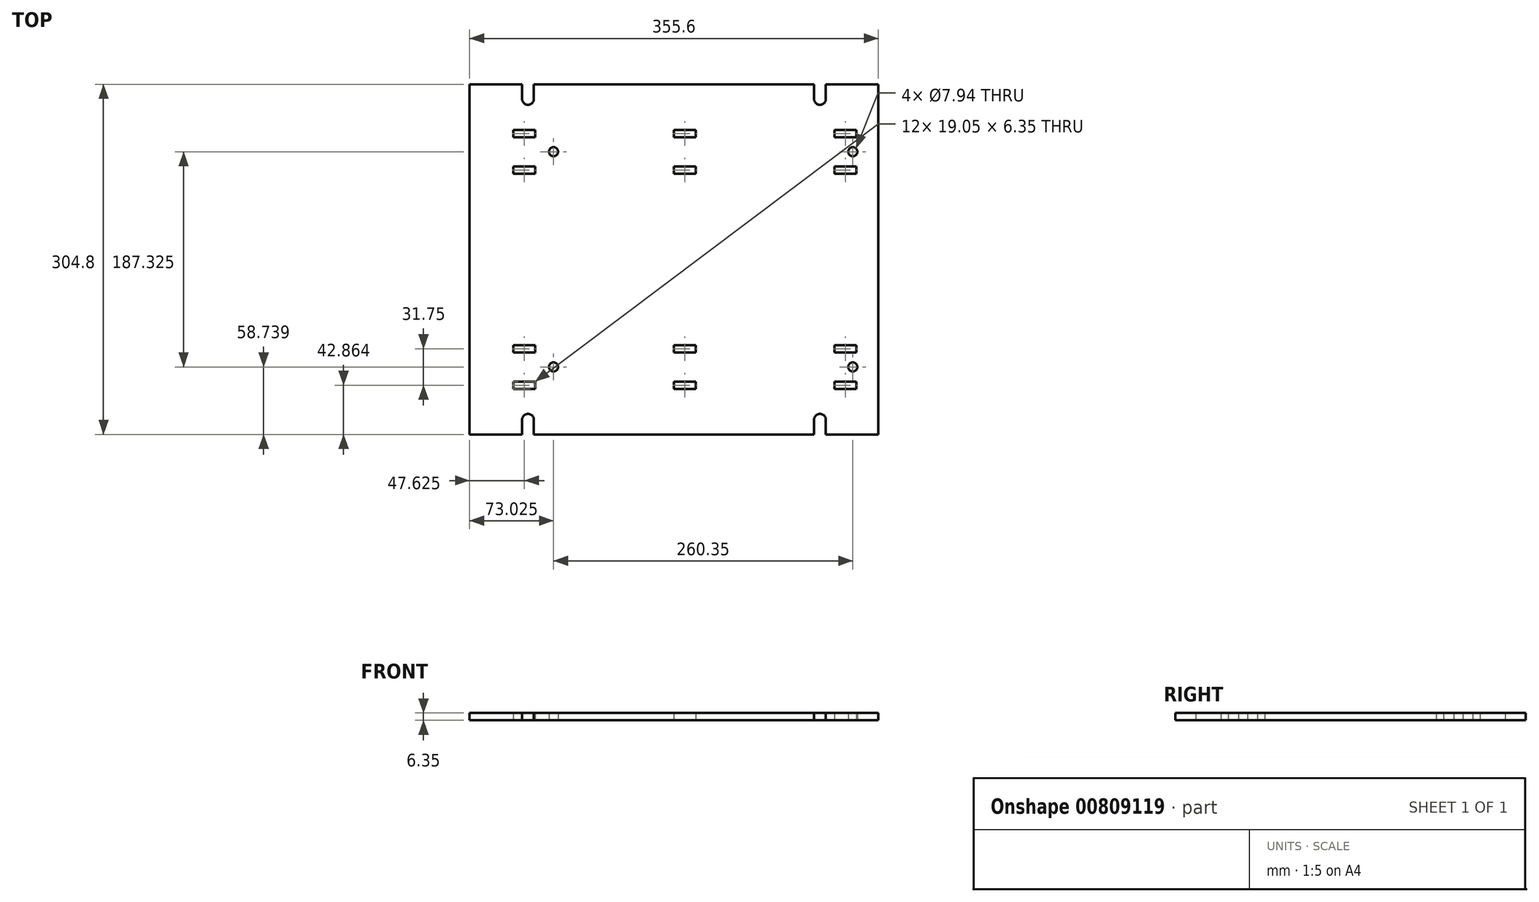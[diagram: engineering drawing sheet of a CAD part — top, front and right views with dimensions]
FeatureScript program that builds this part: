
annotation { "Feature Type Name" : "Feature", "Feature Type Description" : "" }
export const myFeature = defineFeature(function(context is Context, id is Id, definition is map)
    precondition{}
    {
        {
            var Q0;
            Q0=qCreatedBy(makeId("Top.planeOp"),FACE);
            var sketch = newSketch(context, id + "F0", { "sketchPlane" : qUnion([Q0])});
            skLineSegment(sketch, "E0.bottom", {"start": v(0, 4.6) * mm, "end": v(355.6, 4.6) * mm});
            skLineSegment(sketch, "E0.top", {"start": v(0, 309.4) * mm, "end": v(355.6, 309.4) * mm});
            skLineSegment(sketch, "E0.left", {"start": v(0, 4.6) * mm, "end": v(0, 309.4) * mm});
            skLineSegment(sketch, "E0.right", {"start": v(355.6, 4.6) * mm, "end": v(355.6, 309.4) * mm});
            skCircle(sketch, "E1", {"center": v(333.38, 63.33) * mm, "radius": 3.97 * mm});
            skCircle(sketch, "E2.0.1.0", {"center": v(333.38, 250.65) * mm, "radius": 3.97 * mm});
            skCircle(sketch, "E2.1.0.0", {"center": v(73.03, 63.33) * mm, "radius": 3.97 * mm});
            skCircle(sketch, "E2.1.1.0", {"center": v(73.03, 250.65) * mm, "radius": 3.97 * mm});
            skLineSegment(sketch, "E2.direction1", {"start": v(333.38, 63.33) * mm, "end": v(73.03, 63.33) * mm, "construction": true});
            skLineSegment(sketch, "E2.direction2", {"start": v(333.38, 63.33) * mm, "end": v(333.38, 250.65) * mm, "construction": true});
            skLineSegment(sketch, "E3.bottom", {"start": v(336.55, 44.28) * mm, "end": v(317.5, 44.28) * mm});
            skLineSegment(sketch, "E3.top", {"start": v(336.55, 50.63) * mm, "end": v(317.5, 50.63) * mm});
            skLineSegment(sketch, "E3.left", {"start": v(336.55, 44.28) * mm, "end": v(336.55, 50.63) * mm});
            skLineSegment(sketch, "E3.right", {"start": v(317.5, 44.28) * mm, "end": v(317.5, 50.63) * mm});
            skLineSegment(sketch, "E4.0.1.0", {"start": v(336.55, 82.38) * mm, "end": v(317.5, 82.38) * mm});
            skLineSegment(sketch, "E4.0.1.1", {"start": v(336.55, 76.03) * mm, "end": v(317.5, 76.03) * mm});
            skLineSegment(sketch, "E4.0.1.2", {"start": v(317.5, 76.03) * mm, "end": v(317.5, 82.38) * mm});
            skLineSegment(sketch, "E4.0.1.3", {"start": v(336.55, 76.03) * mm, "end": v(336.55, 82.38) * mm});
            skLineSegment(sketch, "E4.direction2", {"start": v(317.5, 50.63) * mm, "end": v(317.5, 82.38) * mm, "construction": true});
            skLineSegment(sketch, "E5.0.1.0", {"start": v(336.55, 269.7) * mm, "end": v(317.5, 269.7) * mm});
            skLineSegment(sketch, "E5.0.1.1", {"start": v(336.55, 263.35) * mm, "end": v(336.55, 269.7) * mm});
            skLineSegment(sketch, "E5.0.1.2", {"start": v(336.55, 263.35) * mm, "end": v(317.5, 263.35) * mm});
            skLineSegment(sketch, "E5.0.1.3", {"start": v(336.55, 231.6) * mm, "end": v(317.5, 231.6) * mm});
            skLineSegment(sketch, "E5.0.1.4", {"start": v(336.55, 231.6) * mm, "end": v(336.55, 237.95) * mm});
            skLineSegment(sketch, "E5.0.1.5", {"start": v(317.5, 231.6) * mm, "end": v(317.5, 237.95) * mm});
            skLineSegment(sketch, "E5.0.1.6", {"start": v(317.5, 263.35) * mm, "end": v(317.5, 269.7) * mm});
            skLineSegment(sketch, "E5.0.1.7", {"start": v(336.55, 237.95) * mm, "end": v(317.5, 237.95) * mm});
            skLineSegment(sketch, "E5.1.0.0", {"start": v(196.85, 82.38) * mm, "end": v(177.8, 82.38) * mm});
            skLineSegment(sketch, "E5.1.0.1", {"start": v(196.85, 76.03) * mm, "end": v(196.85, 82.38) * mm});
            skLineSegment(sketch, "E5.1.0.2", {"start": v(196.85, 76.03) * mm, "end": v(177.8, 76.03) * mm});
            skLineSegment(sketch, "E5.1.0.3", {"start": v(196.85, 44.28) * mm, "end": v(177.8, 44.28) * mm});
            skLineSegment(sketch, "E5.1.0.4", {"start": v(196.85, 44.28) * mm, "end": v(196.85, 50.63) * mm});
            skLineSegment(sketch, "E5.1.0.5", {"start": v(177.8, 44.28) * mm, "end": v(177.8, 50.63) * mm});
            skLineSegment(sketch, "E5.1.0.6", {"start": v(177.8, 76.03) * mm, "end": v(177.8, 82.38) * mm});
            skLineSegment(sketch, "E5.1.0.7", {"start": v(196.85, 50.63) * mm, "end": v(177.8, 50.63) * mm});
            skLineSegment(sketch, "E5.1.1.0", {"start": v(196.85, 269.7) * mm, "end": v(177.8, 269.7) * mm});
            skLineSegment(sketch, "E5.1.1.1", {"start": v(196.85, 263.35) * mm, "end": v(196.85, 269.7) * mm});
            skLineSegment(sketch, "E5.1.1.2", {"start": v(196.85, 263.35) * mm, "end": v(177.8, 263.35) * mm});
            skLineSegment(sketch, "E5.1.1.3", {"start": v(196.85, 231.6) * mm, "end": v(177.8, 231.6) * mm});
            skLineSegment(sketch, "E5.1.1.4", {"start": v(196.85, 231.6) * mm, "end": v(196.85, 237.95) * mm});
            skLineSegment(sketch, "E5.1.1.5", {"start": v(177.8, 231.6) * mm, "end": v(177.8, 237.95) * mm});
            skLineSegment(sketch, "E5.1.1.6", {"start": v(177.8, 263.35) * mm, "end": v(177.8, 269.7) * mm});
            skLineSegment(sketch, "E5.1.1.7", {"start": v(196.85, 237.95) * mm, "end": v(177.8, 237.95) * mm});
            skLineSegment(sketch, "E5.2.0.0", {"start": v(57.15, 82.38) * mm, "end": v(38.1, 82.38) * mm});
            skLineSegment(sketch, "E5.2.0.1", {"start": v(57.15, 76.03) * mm, "end": v(57.15, 82.38) * mm});
            skLineSegment(sketch, "E5.2.0.2", {"start": v(57.15, 76.03) * mm, "end": v(38.1, 76.03) * mm});
            skLineSegment(sketch, "E5.2.0.3", {"start": v(57.15, 44.28) * mm, "end": v(38.1, 44.28) * mm});
            skLineSegment(sketch, "E5.2.0.4", {"start": v(57.15, 44.28) * mm, "end": v(57.15, 50.63) * mm});
            skLineSegment(sketch, "E5.2.0.5", {"start": v(38.1, 44.28) * mm, "end": v(38.1, 50.63) * mm});
            skLineSegment(sketch, "E5.2.0.6", {"start": v(38.1, 76.03) * mm, "end": v(38.1, 82.38) * mm});
            skLineSegment(sketch, "E5.2.0.7", {"start": v(57.15, 50.63) * mm, "end": v(38.1, 50.63) * mm});
            skLineSegment(sketch, "E5.2.1.0", {"start": v(57.15, 269.7) * mm, "end": v(38.1, 269.7) * mm});
            skLineSegment(sketch, "E5.2.1.1", {"start": v(57.15, 263.35) * mm, "end": v(57.15, 269.7) * mm});
            skLineSegment(sketch, "E5.2.1.2", {"start": v(57.15, 263.35) * mm, "end": v(38.1, 263.35) * mm});
            skLineSegment(sketch, "E5.2.1.3", {"start": v(57.15, 231.6) * mm, "end": v(38.1, 231.6) * mm});
            skLineSegment(sketch, "E5.2.1.4", {"start": v(57.15, 231.6) * mm, "end": v(57.15, 237.95) * mm});
            skLineSegment(sketch, "E5.2.1.5", {"start": v(38.1, 231.6) * mm, "end": v(38.1, 237.95) * mm});
            skLineSegment(sketch, "E5.2.1.6", {"start": v(38.1, 263.35) * mm, "end": v(38.1, 269.7) * mm});
            skLineSegment(sketch, "E5.2.1.7", {"start": v(57.15, 237.95) * mm, "end": v(38.1, 237.95) * mm});
            skLineSegment(sketch, "E5.direction1", {"start": v(317.5, 44.28) * mm, "end": v(177.8, 44.28) * mm, "construction": true});
            skLineSegment(sketch, "E5.direction2", {"start": v(317.5, 44.28) * mm, "end": v(317.5, 231.6) * mm, "construction": true});
            skCircle(sketch, "E6", {"center": v(304.8, 17.3) * mm, "radius": 5.16 * mm});
            skLineSegment(sketch, "E7", {"start": v(309.96, 17.3) * mm, "end": v(309.96, 4.6) * mm});
            skLineSegment(sketch, "E8", {"start": v(299.64, 17.3) * mm, "end": v(299.64, 4.6) * mm});
            skLineSegment(sketch, "E9.1.0.0", {"start": v(55.96, 17.3) * mm, "end": v(55.96, 4.6) * mm});
            skLineSegment(sketch, "E9.1.0.1", {"start": v(45.64, 17.3) * mm, "end": v(45.64, 4.6) * mm});
            skCircle(sketch, "E9.1.0.2", {"center": v(50.8, 17.3) * mm, "radius": 5.16 * mm});
            skLineSegment(sketch, "E9.direction1", {"start": v(309.96, 4.6) * mm, "end": v(55.96, 4.6) * mm, "construction": true});
            skLineSegment(sketch, "E10", {"start": v(355.6, 157) * mm, "end": v(386.25, 157) * mm, "construction": true});
            skCircle(sketch, "E11.MirrorC", {"center": v(304.8, 296.7) * mm, "radius": 5.16 * mm});
            skLineSegment(sketch, "E12.MirrorCS", {"start": v(309.96, 296.7) * mm, "end": v(309.96, 309.4) * mm});
            skLineSegment(sketch, "E13.MirrorCS", {"start": v(299.64, 296.7) * mm, "end": v(299.64, 309.4) * mm});
            skCircle(sketch, "E14.MirrorC", {"center": v(50.8, 296.7) * mm, "radius": 5.16 * mm});
            skLineSegment(sketch, "E15.MirrorCS", {"start": v(45.64, 296.7) * mm, "end": v(45.64, 309.4) * mm});
            skLineSegment(sketch, "E16.MirrorCS", {"start": v(55.96, 296.7) * mm, "end": v(55.96, 309.4) * mm});
            skSolve(sketch);
        }
        {
            var Q0;
            Q0=makeQuery(id+"F0.imprint","IMPRINT",FACE,{"disambiguationData":[TD([[makeQuery(id+"F0.imprint","IMPRINT",EDGE,{"derivedFrom":sQuery(id+"F0.wireOp",EDGE,"E0.top")}),-1.0]])]});
            extrude(context, id + "F1", {"entities" : qUnion([Q0]), "depth" : 6.35 * mm, "offsetDistance" : 25.4 * mm});
        }
    });
